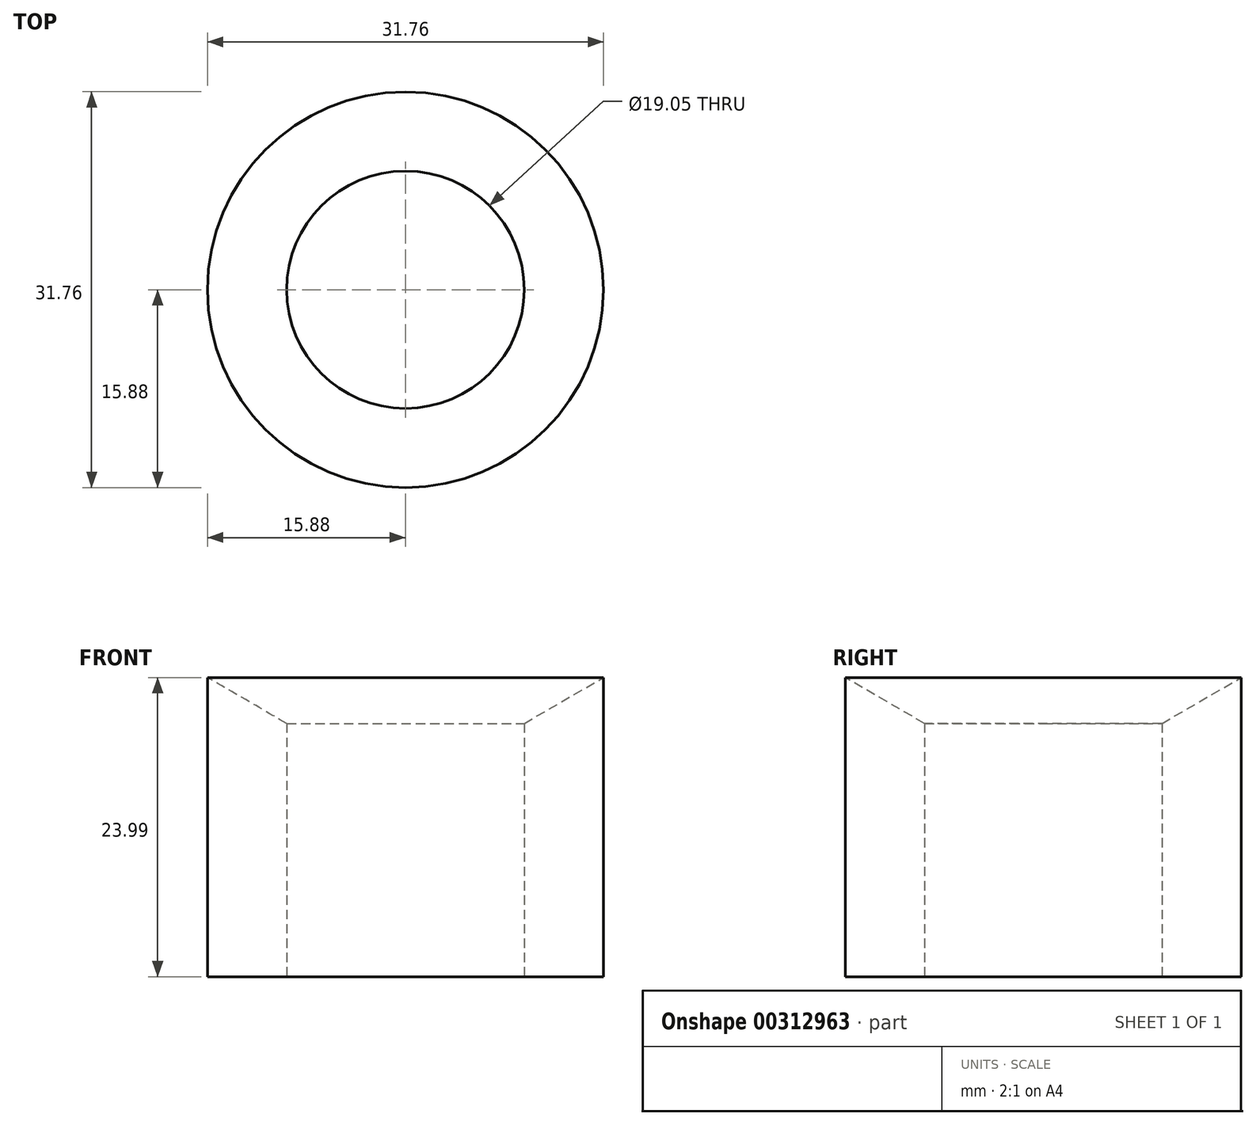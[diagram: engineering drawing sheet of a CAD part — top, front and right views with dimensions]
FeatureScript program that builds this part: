
annotation { "Feature Type Name" : "Feature", "Feature Type Description" : "" }
export const myFeature = defineFeature(function(context is Context, id is Id, definition is map)
    precondition{}
    {
        {
            var Q0;
            Q0=qCreatedBy(makeId("Front.planeOp"),FACE);
            var sketch = newSketch(context, id + "F0", { "sketchPlane" : qUnion([Q0])});
            skLineSegment(sketch, "E0", {"start": v(-9.53, 20.32) * mm, "end": v(-9.52, 0) * mm});
            skLineSegment(sketch, "E1", {"start": v(-9.52, 0) * mm, "end": v(-15.88, 0) * mm});
            skLineSegment(sketch, "E2", {"start": v(-15.88, 0) * mm, "end": v(-15.88, 23.99) * mm});
            skLineSegment(sketch, "E3", {"start": v(-15.88, 23.99) * mm, "end": v(-9.53, 20.32) * mm});
            skLineSegment(sketch, "E4", {"start": v(0, 0) * mm, "end": v(0, 15.46) * mm, "construction": true});
            skSolve(sketch);
        }
        {
            var Q0;
            Q0=qSketchRegion(id+"F0",true);
            var Q1;
            Q1=sQuery(id+"F0.wireOp",EDGE,"E4");
            revolve(context, id + "F1", {"entities" : qUnion([Q0]), "axis" : qUnion([Q1]), "revolveType" : RevolveType.FULL});
        }
    });
